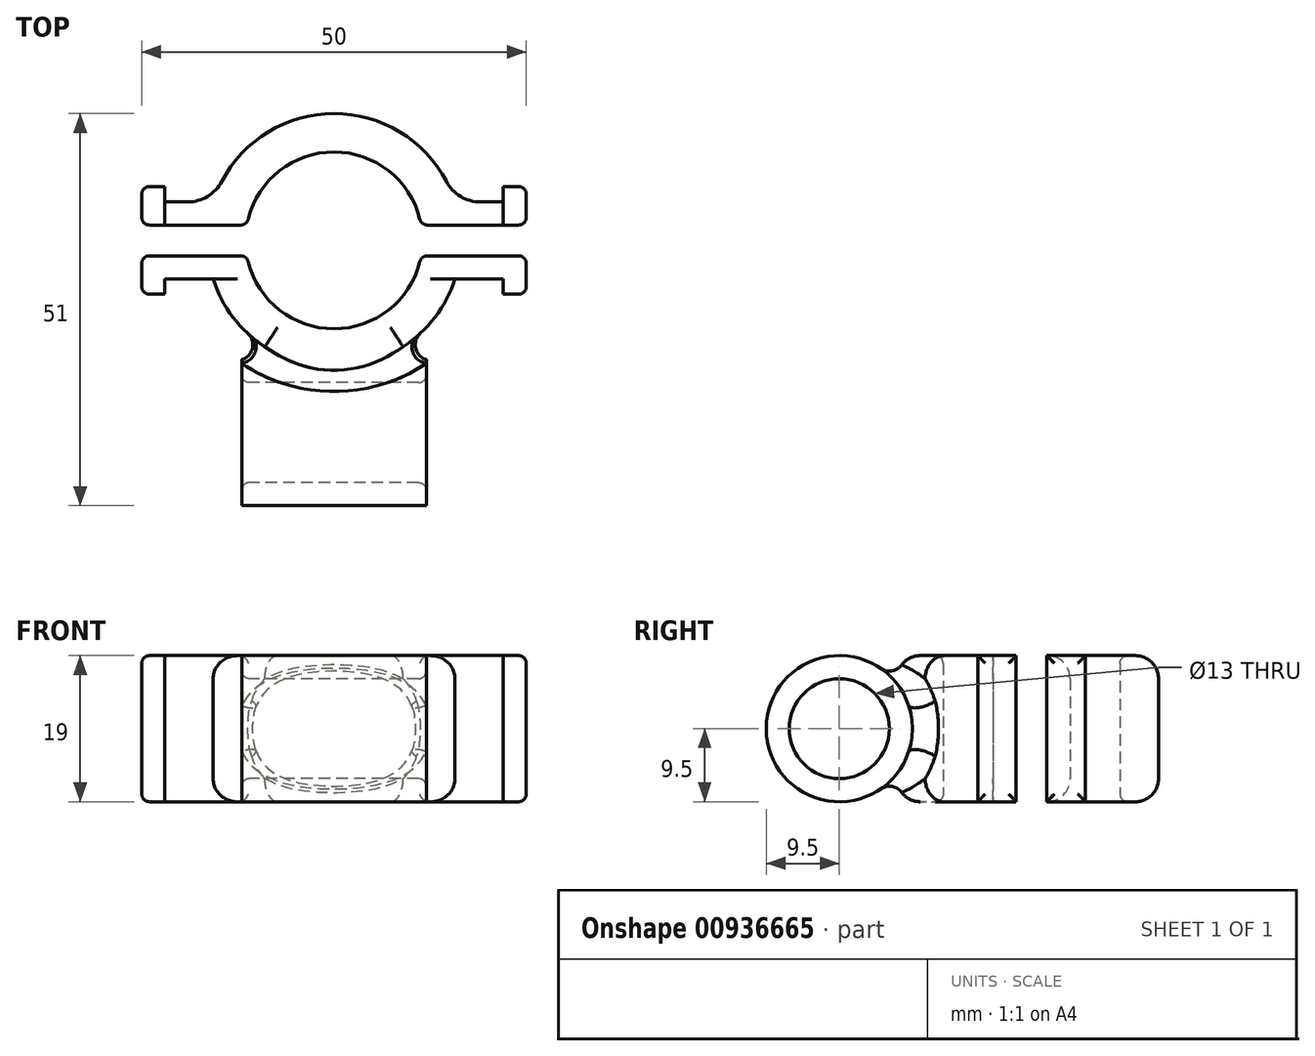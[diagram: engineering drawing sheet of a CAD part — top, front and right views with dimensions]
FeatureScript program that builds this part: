
annotation { "Feature Type Name" : "Feature", "Feature Type Description" : "" }
export const myFeature = defineFeature(function(context is Context, id is Id, definition is map)
    precondition{}
    {
        {
            var Q0;
            Q0=qCreatedBy(makeId("Top.planeOp"),FACE);
            var sketch = newSketch(context, id + "F0", { "sketchPlane" : qUnion([Q0])});
            skCircle(sketch, "E0", {"center": v(0, 0) * mm, "radius": 11.5 * mm});
            skCircle(sketch, "E1.0", {"center": v(0, 0) * mm, "radius": 16.5 * mm});
            skSolve(sketch);
        }
        {
            var Q0;
            Q0=qCreatedBy(makeId("Right.planeOp"),FACE);
            var sketch = newSketch(context, id + "F1", { "sketchPlane" : qUnion([Q0])});
            skCircle(sketch, "E2", {"center": v(-25, 0) * mm, "radius": 6.5 * mm});
            skCircle(sketch, "E3.0", {"center": v(-25, 0) * mm, "radius": 9.5 * mm});
            skSolve(sketch);
        }
        {
            var Q0;
            Q0=makeQuery(id+"F0.imprint","IMPRINT",FACE,{"disambiguationData":[TD([[makeQuery(id+"F0.imprint","IMPRINT",EDGE,{"derivedFrom":sQuery(id+"F0.wireOp",EDGE,"E0")}),-1.0]])]});
            extrude(context, id + "F2", {"entities" : qUnion([Q0]), "endBound" : BoundingType.SYMMETRIC, "depth" : 19 * mm, "offsetDistance" : 25 * mm});
        }
        {
            var Q0;
            Q0=makeQuery(id+"F1.imprint","IMPRINT",FACE,{"disambiguationData":[TD([[makeQuery(id+"F1.imprint","IMPRINT",EDGE,{"derivedFrom":sQuery(id+"F1.wireOp",EDGE,"E2")}),-1.0]])]});
            extrude(context, id + "F3", {"entities" : qUnion([Q0]), "operationType" : NewBodyOperationType.ADD, "endBound" : BoundingType.SYMMETRIC, "depth" : 24 * mm, "offsetDistance" : 25 * mm});
        }
        {
            var Q0;
            Q0=qCreatedBy(makeId("Top.planeOp"),FACE);
            var sketch = newSketch(context, id + "F4", { "sketchPlane" : qUnion([Q0])});
            skLineSegment(sketch, "E4.bottom", {"start": v(-17.56, -2) * mm, "end": v(17.56, -2) * mm});
            skLineSegment(sketch, "E4.top", {"start": v(-17.56, 2) * mm, "end": v(17.56, 2) * mm});
            skLineSegment(sketch, "E4.left", {"start": v(-17.56, -2) * mm, "end": v(-17.56, 2) * mm});
            skLineSegment(sketch, "E4.right", {"start": v(17.56, -2) * mm, "end": v(17.56, 2) * mm});
            skPoint(sketch, "E4.middle", {"position": v(0, 0) * mm});
            skSolve(sketch);
        }
        {
            var Q0;
            Q0=makeQuery(id+"F4.imprint","IMPRINT",FACE,{"disambiguationData":[TD([[makeQuery(id+"F4.imprint","IMPRINT",EDGE,{"derivedFrom":sQuery(id+"F4.wireOp",EDGE,"E4.bottom")}),1.0]])]});
            var Q1;
            Q1=makeQuery(id+"F2.opExtrude","CAP_FACE",FACE,{"disambiguationData":[OSD([sQuery(id+"F0.wireOp",EDGE,"E0"),sQuery(id+"F0.wireOp",EDGE,"E1.0")])],"isStart":false});
            extrude(context, id + "F5", {"entities" : qUnion([Q0]), "operationType" : NewBodyOperationType.REMOVE, "endBound" : BoundingType.SYMMETRIC, "depth" : 25 * mm, "endBoundEntityFace" : qUnion([Q1]), "offsetDistance" : 25 * mm});
        }
        {
            var Q0;
            {var subQ0=sQuery(id+"F0.wireOp",EDGE,"E0");var subQ1=sQuery(id+"F0.wireOp",EDGE,"E1.0");Q0=makeQuery(id+"F5.boolean.opBoolean","SPLIT",FACE,{"disambiguationData":[TD([makeQuery(id+"F5.opExtrude","SWEPT_FACE",FACE,{"disambiguationData":[OSD([sQuery(id+"F4.wireOp",EDGE,"E4.bottom")])]})])],"derivedFrom":makeQuery(id+"F2.opExtrude","CAP_FACE",FACE,{"disambiguationData":[OSD([subQ0,subQ1])],"isStart":true})});}
            var sketch = newSketch(context, id + "F6", { "sketchPlane" : qUnion([Q0])});
            skLineSegment(sketch, "E5.bottom", {"start": v(-25, 5) * mm, "end": v(25, 5) * mm});
            skLineSegment(sketch, "E5.top", {"start": v(-25, -5) * mm, "end": v(25, -5) * mm});
            skLineSegment(sketch, "E5.left", {"start": v(-25, 5) * mm, "end": v(-25, -5) * mm});
            skLineSegment(sketch, "E5.right", {"start": v(25, 5) * mm, "end": v(25, -5) * mm});
            skPoint(sketch, "E5.middle", {"position": v(0, 0) * mm});
            skArc(sketch, "E6", {"start": v(11.32, 2) * mm, "mid": v(0, 11.5) * mm, "end": v(-11.32, 2) * mm});
            skLineSegment(sketch, "E7.bottom", {"start": v(-19, 2) * mm, "end": v(19, 2) * mm});
            skLineSegment(sketch, "E7.top", {"start": v(-19, -2) * mm, "end": v(19, -2) * mm});
            skLineSegment(sketch, "E7.left", {"start": v(-19, 2) * mm, "end": v(-19, -2) * mm});
            skLineSegment(sketch, "E7.right", {"start": v(19, 2) * mm, "end": v(19, -2) * mm});
            skArc(sketch, "E8.trimOffspring", {"start": v(-11.32, -2) * mm, "mid": v(0, -11.5) * mm, "end": v(11.32, -2) * mm});
            skLineSegment(sketch, "E9", {"start": v(19, -2) * mm, "end": v(25, -2) * mm});
            skLineSegment(sketch, "E10", {"start": v(19, 2) * mm, "end": v(25, 2) * mm});
            skLineSegment(sketch, "E11", {"start": v(-19, -2) * mm, "end": v(-25, -2) * mm});
            skLineSegment(sketch, "E12", {"start": v(-19, 2) * mm, "end": v(-25, 2) * mm});
            skLineSegment(sketch, "E13.bottom", {"start": v(-25, 5) * mm, "end": v(-22, 5) * mm});
            skLineSegment(sketch, "E13.top", {"start": v(-25, 7) * mm, "end": v(-22, 7) * mm});
            skLineSegment(sketch, "E13.left", {"start": v(-25, 5) * mm, "end": v(-25, 7) * mm});
            skLineSegment(sketch, "E13.right", {"start": v(-22, 5) * mm, "end": v(-22, 7) * mm});
            skLineSegment(sketch, "E14.bottom", {"start": v(-25, -5) * mm, "end": v(-22, -5) * mm});
            skLineSegment(sketch, "E14.top", {"start": v(-25, -7) * mm, "end": v(-22, -7) * mm});
            skLineSegment(sketch, "E14.left", {"start": v(-25, -5) * mm, "end": v(-25, -7) * mm});
            skLineSegment(sketch, "E14.right", {"start": v(-22, -5) * mm, "end": v(-22, -7) * mm});
            skPoint(sketch, "E15.oppositeSnap0", {"position": v(22, -2) * mm});
            skLineSegment(sketch, "E15.bottom", {"start": v(25, -5) * mm, "end": v(22, -5) * mm});
            skLineSegment(sketch, "E15.top", {"start": v(25, -7) * mm, "end": v(22, -7) * mm});
            skLineSegment(sketch, "E15.left", {"start": v(25, -5) * mm, "end": v(25, -7) * mm});
            skLineSegment(sketch, "E15.right", {"start": v(22, -5) * mm, "end": v(22, -7) * mm});
            skLineSegment(sketch, "E16.bottom", {"start": v(25, 5) * mm, "end": v(22, 5) * mm});
            skLineSegment(sketch, "E16.top", {"start": v(25, 7) * mm, "end": v(22, 7) * mm});
            skLineSegment(sketch, "E16.left", {"start": v(25, 5) * mm, "end": v(25, 7) * mm});
            skLineSegment(sketch, "E16.right", {"start": v(22, 5) * mm, "end": v(22, 7) * mm});
            skSolve(sketch);
        }
        {
            var Q0;
            {var subQ0=sQuery(id+"F6.wireOp",EDGE,"E9");Q0=makeQuery(id+"F6.imprint","IMPRINT",FACE,{"disambiguationData":[TD([[makeQuery(id+"F6.imprint","IMPRINT",EDGE,{"derivedFrom":subQ0}),-1.0]])]});}
            var Q1;
            {var subQ4=sQuery(id+"F6.wireOp",EDGE,"E10");Q1=makeQuery(id+"F6.imprint","IMPRINT",FACE,{"disambiguationData":[TD([[makeQuery(id+"F6.imprint","IMPRINT",EDGE,{"derivedFrom":subQ4}),1.0]])]});}
            var Q2;
            {var subQ4=sQuery(id+"F6.wireOp",EDGE,"E12");Q2=makeQuery(id+"F6.imprint","IMPRINT",FACE,{"disambiguationData":[TD([[makeQuery(id+"F6.imprint","IMPRINT",EDGE,{"derivedFrom":subQ4}),-1.0]])]});}
            var Q3;
            {var subQ3=sQuery(id+"F6.wireOp",EDGE,"E11");Q3=makeQuery(id+"F6.imprint","IMPRINT",FACE,{"disambiguationData":[TD([[makeQuery(id+"F6.imprint","IMPRINT",EDGE,{"derivedFrom":subQ3}),1.0]])]});}
            var Q4;
            Q4=makeQuery(id+"F6.imprint","IMPRINT",FACE,{"disambiguationData":[TD([[makeQuery(id+"F6.imprint","IMPRINT",EDGE,{"derivedFrom":sQuery(id+"F6.wireOp",EDGE,"E13.top")}),-1.0]])]});
            var Q5;
            Q5=makeQuery(id+"F6.imprint","IMPRINT",FACE,{"disambiguationData":[TD([[makeQuery(id+"F6.imprint","IMPRINT",EDGE,{"derivedFrom":sQuery(id+"F6.wireOp",EDGE,"E14.top")}),1.0]])]});
            var Q6;
            Q6=makeQuery(id+"F6.imprint","IMPRINT",FACE,{"disambiguationData":[TD([[makeQuery(id+"F6.imprint","IMPRINT",EDGE,{"derivedFrom":sQuery(id+"F6.wireOp",EDGE,"E15.top")}),-1.0]])]});
            var Q7;
            Q7=makeQuery(id+"F6.imprint","IMPRINT",FACE,{"disambiguationData":[TD([[makeQuery(id+"F6.imprint","IMPRINT",EDGE,{"derivedFrom":sQuery(id+"F6.wireOp",EDGE,"E16.top")}),1.0]])]});
            var Q8;
            {var subQ0=sQuery(id+"F0.wireOp",EDGE,"E0");var subQ1=sQuery(id+"F0.wireOp",EDGE,"E1.0");Q8=makeQuery(id+"F5.boolean.opBoolean","SPLIT",FACE,{"disambiguationData":[TD([makeQuery(id+"F5.opExtrude","SWEPT_FACE",FACE,{"disambiguationData":[OSD([sQuery(id+"F4.wireOp",EDGE,"E4.top")])]})])],"derivedFrom":makeQuery(id+"F2.opExtrude","CAP_FACE",FACE,{"disambiguationData":[OSD([subQ0,subQ1])],"isStart":false})});}
            extrude(context, id + "F7", {"entities" : qUnion([Q0, Q1, Q2, Q3, Q4, Q5, Q6, Q7]), "operationType" : NewBodyOperationType.ADD, "endBound" : BoundingType.UP_TO_SURFACE, "oppositeDirection" : true, "depth" : 25 * mm, "endBoundEntityFace" : qUnion([Q8]), "offsetDistance" : 25 * mm});
        }
        {
            var Q0;
            Q0=makeQuery(id+"F3.boolean.opBoolean","INTERSECT",EDGE,{"derivedFrom":[makeQuery(id+"F2.opExtrude","SWEPT_FACE",FACE,{"disambiguationData":[OSD([sQuery(id+"F0.wireOp",EDGE,"E1.0")])]}),makeQuery(id+"F3.opExtrude","SWEPT_FACE",FACE,{"disambiguationData":[OSD([sQuery(id+"F1.wireOp",EDGE,"E3.0")])]})]});
            fillet(context, id + "F8", {"entities" : qUnion([Q0]), "radius" : 2 * mm, "tangentPropagation" : true, "allowEdgeOverflow" : false});
        }
        {
            var Q0;
            Q0=makeQuery(id+"F3.opExtrude","CAP_EDGE",EDGE,{"disambiguationData":[OSD([sQuery(id+"F1.wireOp",EDGE,"E2")])],"isStart":false});
            var Q1;
            Q1=makeQuery(id+"F3.opExtrude","CAP_EDGE",EDGE,{"disambiguationData":[OSD([sQuery(id+"F1.wireOp",EDGE,"E2")])],"isStart":true});
            var Q2;
            {var subQ0=sQuery(id+"F0.wireOp",EDGE,"E0");Q2=makeQuery(id+"F5.boolean.opBoolean","SPLIT",EDGE,{"disambiguationData":[TD([makeQuery(id+"F5.opExtrude","SWEPT_FACE",FACE,{"disambiguationData":[OSD([sQuery(id+"F4.wireOp",EDGE,"E4.bottom")])]})])],"derivedFrom":makeQuery(id+"F2.opExtrude","CAP_EDGE",EDGE,{"disambiguationData":[OSD([subQ0])],"isStart":false})});}
            var Q3;
            {var subQ0=sQuery(id+"F0.wireOp",EDGE,"E0");Q3=makeQuery(id+"F5.boolean.opBoolean","SPLIT",EDGE,{"disambiguationData":[TD([makeQuery(id+"F5.opExtrude","SWEPT_FACE",FACE,{"disambiguationData":[OSD([sQuery(id+"F4.wireOp",EDGE,"E4.top")])]})])],"derivedFrom":makeQuery(id+"F2.opExtrude","CAP_EDGE",EDGE,{"disambiguationData":[OSD([subQ0])],"isStart":false})});}
            var Q4;
            {var subQ0=sQuery(id+"F0.wireOp",EDGE,"E0");Q4=makeQuery(id+"F5.boolean.opBoolean","SPLIT",EDGE,{"disambiguationData":[TD([makeQuery(id+"F5.opExtrude","SWEPT_FACE",FACE,{"disambiguationData":[OSD([sQuery(id+"F4.wireOp",EDGE,"E4.bottom")])]})])],"derivedFrom":makeQuery(id+"F2.opExtrude","CAP_EDGE",EDGE,{"disambiguationData":[OSD([subQ0])],"isStart":true})});}
            var Q5;
            {var subQ0=sQuery(id+"F0.wireOp",EDGE,"E0");Q5=makeQuery(id+"F5.boolean.opBoolean","SPLIT",EDGE,{"disambiguationData":[TD([makeQuery(id+"F5.opExtrude","SWEPT_FACE",FACE,{"disambiguationData":[OSD([sQuery(id+"F4.wireOp",EDGE,"E4.top")])]})])],"derivedFrom":makeQuery(id+"F2.opExtrude","CAP_EDGE",EDGE,{"disambiguationData":[OSD([subQ0])],"isStart":true})});}
            var Q6;
            Q6=makeQuery(id+"F5.boolean.opBoolean","INTERSECT",EDGE,{"disambiguationData":[OD(1.0)],"derivedFrom":[makeQuery(id+"F2.opExtrude","SWEPT_FACE",FACE,{"disambiguationData":[OSD([sQuery(id+"F0.wireOp",EDGE,"E0")])]}),makeQuery(id+"F5.opExtrude","SWEPT_FACE",FACE,{"disambiguationData":[OSD([sQuery(id+"F4.wireOp",EDGE,"E4.top")])]})]});
            var Q7;
            Q7=makeQuery(id+"F5.boolean.opBoolean","INTERSECT",EDGE,{"disambiguationData":[OD(1.0)],"derivedFrom":[makeQuery(id+"F2.opExtrude","SWEPT_FACE",FACE,{"disambiguationData":[OSD([sQuery(id+"F0.wireOp",EDGE,"E0")])]}),makeQuery(id+"F5.opExtrude","SWEPT_FACE",FACE,{"disambiguationData":[OSD([sQuery(id+"F4.wireOp",EDGE,"E4.bottom")])]})]});
            var Q8;
            Q8=makeQuery(id+"F5.boolean.opBoolean","INTERSECT",EDGE,{"disambiguationData":[OD(0.0)],"derivedFrom":[makeQuery(id+"F2.opExtrude","SWEPT_FACE",FACE,{"disambiguationData":[OSD([sQuery(id+"F0.wireOp",EDGE,"E0")])]}),makeQuery(id+"F5.opExtrude","SWEPT_FACE",FACE,{"disambiguationData":[OSD([sQuery(id+"F4.wireOp",EDGE,"E4.bottom")])]})]});
            var Q9;
            Q9=makeQuery(id+"F5.boolean.opBoolean","INTERSECT",EDGE,{"disambiguationData":[OD(0.0)],"derivedFrom":[makeQuery(id+"F2.opExtrude","SWEPT_FACE",FACE,{"disambiguationData":[OSD([sQuery(id+"F0.wireOp",EDGE,"E0")])]}),makeQuery(id+"F5.opExtrude","SWEPT_FACE",FACE,{"disambiguationData":[OSD([sQuery(id+"F4.wireOp",EDGE,"E4.top")])]})]});
            fillet(context, id + "F9", {"entities" : qUnion([Q0, Q1, Q2, Q3, Q4, Q5, Q6, Q7, Q8, Q9]), "radius" : 1 * mm, "tangentPropagation" : true, "allowEdgeOverflow" : false});
        }
        {
            var Q0;
            {var subQ0=sQuery(id+"F6.wireOp",EDGE,"E5.top");var subQ1=sQuery(id+"F0.wireOp",EDGE,"E1.0");Q0=makeQuery(id+"F7.boolean.opBoolean","INTERSECT",EDGE,{"derivedFrom":[makeQuery(id+"F5.boolean.opBoolean","SPLIT",FACE,{"disambiguationData":[TD([makeQuery(id+"F5.opExtrude","SWEPT_FACE",FACE,{"disambiguationData":[OSD([sQuery(id+"F4.wireOp",EDGE,"E4.top")])]})])],"derivedFrom":makeQuery(id+"F2.opExtrude","SWEPT_FACE",FACE,{"disambiguationData":[OSD([subQ1])]})}),makeQuery(id+"F7.opExtrude","SWEPT_FACE",FACE,{"disambiguationData":[OSD([subQ0]),TDD([makeQuery(id+"F6.imprint","IMPRINT",EDGE,{"disambiguationData":[TD([[makeQuery(id+"F6.imprint","INTERSECT",VERTEX,{"disambiguationData":[OD(0.0)],"derivedFrom":[subQ0,sQuery(id+"F6.wireOp",EDGE,"E8.trimOffspring")]}),1.0]])],"derivedFrom":subQ0})])]})]});}
            var Q1;
            {var subQ0=sQuery(id+"F6.wireOp",EDGE,"E5.bottom");var subQ1=sQuery(id+"F0.wireOp",EDGE,"E1.0");Q1=makeQuery(id+"F7.opExtrude","SWEPT_EDGE",EDGE,{"disambiguationData":[OSD([subQ1,subQ0]),TDD([makeQuery(id+"F6.imprint","INTERSECT",VERTEX,{"disambiguationData":[OD(1.0)],"derivedFrom":[makeQuery(id+"F5.boolean.opBoolean","SPLIT",EDGE,{"disambiguationData":[TD([makeQuery(id+"F5.opExtrude","SWEPT_FACE",FACE,{"disambiguationData":[OSD([sQuery(id+"F4.wireOp",EDGE,"E4.bottom")])]})])],"derivedFrom":makeQuery(id+"F2.opExtrude","CAP_EDGE",EDGE,{"disambiguationData":[OSD([subQ1])],"isStart":true})}),subQ0]})])]});}
            var Q2;
            {var subQ0=sQuery(id+"F6.wireOp",EDGE,"E5.bottom");var subQ1=sQuery(id+"F0.wireOp",EDGE,"E1.0");Q2=makeQuery(id+"F7.opExtrude","SWEPT_EDGE",EDGE,{"disambiguationData":[OSD([subQ1,subQ0]),TDD([makeQuery(id+"F6.imprint","INTERSECT",VERTEX,{"disambiguationData":[OD(0.0)],"derivedFrom":[makeQuery(id+"F5.boolean.opBoolean","SPLIT",EDGE,{"disambiguationData":[TD([makeQuery(id+"F5.opExtrude","SWEPT_FACE",FACE,{"disambiguationData":[OSD([sQuery(id+"F4.wireOp",EDGE,"E4.bottom")])]})])],"derivedFrom":makeQuery(id+"F2.opExtrude","CAP_EDGE",EDGE,{"disambiguationData":[OSD([subQ1])],"isStart":true})}),subQ0]})])]});}
            var Q3;
            {var subQ0=sQuery(id+"F6.wireOp",EDGE,"E5.top");var subQ1=sQuery(id+"F0.wireOp",EDGE,"E1.0");Q3=makeQuery(id+"F7.boolean.opBoolean","INTERSECT",EDGE,{"derivedFrom":[makeQuery(id+"F5.boolean.opBoolean","SPLIT",FACE,{"disambiguationData":[TD([makeQuery(id+"F5.opExtrude","SWEPT_FACE",FACE,{"disambiguationData":[OSD([sQuery(id+"F4.wireOp",EDGE,"E4.top")])]})])],"derivedFrom":makeQuery(id+"F2.opExtrude","SWEPT_FACE",FACE,{"disambiguationData":[OSD([subQ1])]})}),makeQuery(id+"F7.opExtrude","SWEPT_FACE",FACE,{"disambiguationData":[OSD([subQ0]),TDD([makeQuery(id+"F6.imprint","IMPRINT",EDGE,{"disambiguationData":[TD([[makeQuery(id+"F6.imprint","INTERSECT",VERTEX,{"derivedFrom":[subQ0,sQuery(id+"F6.wireOp",EDGE,"E15.right")]}),1.0]])],"derivedFrom":subQ0})])]})]});}
            fillet(context, id + "F10", {"entities" : qUnion([Q0, Q1, Q2, Q3]), "radius" : 5 * mm, "tangentPropagation" : true, "allowEdgeOverflow" : false});
        }
        {
            var Q0;
            {var subQ0=sQuery(id+"F0.wireOp",EDGE,"E1.0");Q0=makeQuery(id+"F5.boolean.opBoolean","SPLIT",EDGE,{"disambiguationData":[TD([makeQuery(id+"F5.opExtrude","SWEPT_FACE",FACE,{"disambiguationData":[OSD([sQuery(id+"F4.wireOp",EDGE,"E4.top")])]})])],"derivedFrom":makeQuery(id+"F2.opExtrude","CAP_EDGE",EDGE,{"disambiguationData":[OSD([subQ0])],"isStart":false})});}
            var Q1;
            {var subQ0=sQuery(id+"F0.wireOp",EDGE,"E1.0");Q1=makeQuery(id+"F5.boolean.opBoolean","SPLIT",EDGE,{"disambiguationData":[TD([makeQuery(id+"F5.opExtrude","SWEPT_FACE",FACE,{"disambiguationData":[OSD([sQuery(id+"F4.wireOp",EDGE,"E4.top")])]})])],"derivedFrom":makeQuery(id+"F2.opExtrude","CAP_EDGE",EDGE,{"disambiguationData":[OSD([subQ0])],"isStart":true})});}
            var Q2;
            {var subQ0=sQuery(id+"F0.wireOp",EDGE,"E1.0");Q2=makeQuery(id+"F5.boolean.opBoolean","SPLIT",EDGE,{"disambiguationData":[TD([makeQuery(id+"F5.opExtrude","SWEPT_FACE",FACE,{"disambiguationData":[OSD([sQuery(id+"F4.wireOp",EDGE,"E4.bottom")])]})])],"derivedFrom":makeQuery(id+"F2.opExtrude","CAP_EDGE",EDGE,{"disambiguationData":[OSD([subQ0])],"isStart":false})});}
            var Q3;
            {var subQ0=sQuery(id+"F0.wireOp",EDGE,"E1.0");Q3=makeQuery(id+"F5.boolean.opBoolean","SPLIT",EDGE,{"disambiguationData":[TD([makeQuery(id+"F5.opExtrude","SWEPT_FACE",FACE,{"disambiguationData":[OSD([sQuery(id+"F4.wireOp",EDGE,"E4.bottom")])]})])],"derivedFrom":makeQuery(id+"F2.opExtrude","CAP_EDGE",EDGE,{"disambiguationData":[OSD([subQ0])],"isStart":true})});}
            var Q4;
            {var subQ0=sQuery(id+"F6.wireOp",EDGE,"E5.top");Q4=makeQuery(id+"F7.opExtrude","CAP_EDGE",EDGE,{"disambiguationData":[OSD([subQ0]),TDD([makeQuery(id+"F6.imprint","IMPRINT",EDGE,{"disambiguationData":[TD([[makeQuery(id+"F6.imprint","INTERSECT",VERTEX,{"disambiguationData":[OD(0.0)],"derivedFrom":[subQ0,sQuery(id+"F6.wireOp",EDGE,"E8.trimOffspring")]}),1.0]])],"derivedFrom":subQ0})])],"isStart":true});}
            var Q5;
            {var subQ0=sQuery(id+"F6.wireOp",EDGE,"E5.top");Q5=makeQuery(id+"F7.opExtrude","CAP_EDGE",EDGE,{"disambiguationData":[OSD([subQ0]),TDD([makeQuery(id+"F6.imprint","IMPRINT",EDGE,{"disambiguationData":[TD([[makeQuery(id+"F6.imprint","INTERSECT",VERTEX,{"disambiguationData":[OD(0.0)],"derivedFrom":[subQ0,sQuery(id+"F6.wireOp",EDGE,"E8.trimOffspring")]}),1.0]])],"derivedFrom":subQ0})])],"isStart":false});}
            fillet(context, id + "F11", {"entities" : qUnion([Q0, Q1, Q2, Q3, Q4, Q5]), "radius" : 3 * mm, "tangentPropagation" : true, "allowEdgeOverflow" : false});
        }
        {
            var Q0;
            Q0=makeQuery(id+"F7.opExtrude","SWEPT_FACE",FACE,{"disambiguationData":[OSD([sQuery(id+"F6.wireOp",EDGE,"E5.right"),sQuery(id+"F6.wireOp",EDGE,"E15.left")])]});
            var Q1;
            Q1=makeQuery(id+"F7.opExtrude","SWEPT_FACE",FACE,{"disambiguationData":[OSD([sQuery(id+"F6.wireOp",EDGE,"E5.right"),sQuery(id+"F6.wireOp",EDGE,"E16.left")])]});
            var Q2;
            Q2=makeQuery(id+"F7.opExtrude","SWEPT_FACE",FACE,{"disambiguationData":[OSD([sQuery(id+"F6.wireOp",EDGE,"E5.left"),sQuery(id+"F6.wireOp",EDGE,"E14.left")])]});
            var Q3;
            Q3=makeQuery(id+"F7.opExtrude","SWEPT_FACE",FACE,{"disambiguationData":[OSD([sQuery(id+"F6.wireOp",EDGE,"E5.left"),sQuery(id+"F6.wireOp",EDGE,"E13.left")])]});
            fillet(context, id + "F12", {"entities" : qUnion([Q0, Q1, Q2, Q3]), "radius" : 1 * mm, "tangentPropagation" : true, "allowEdgeOverflow" : false});
        }
    });
